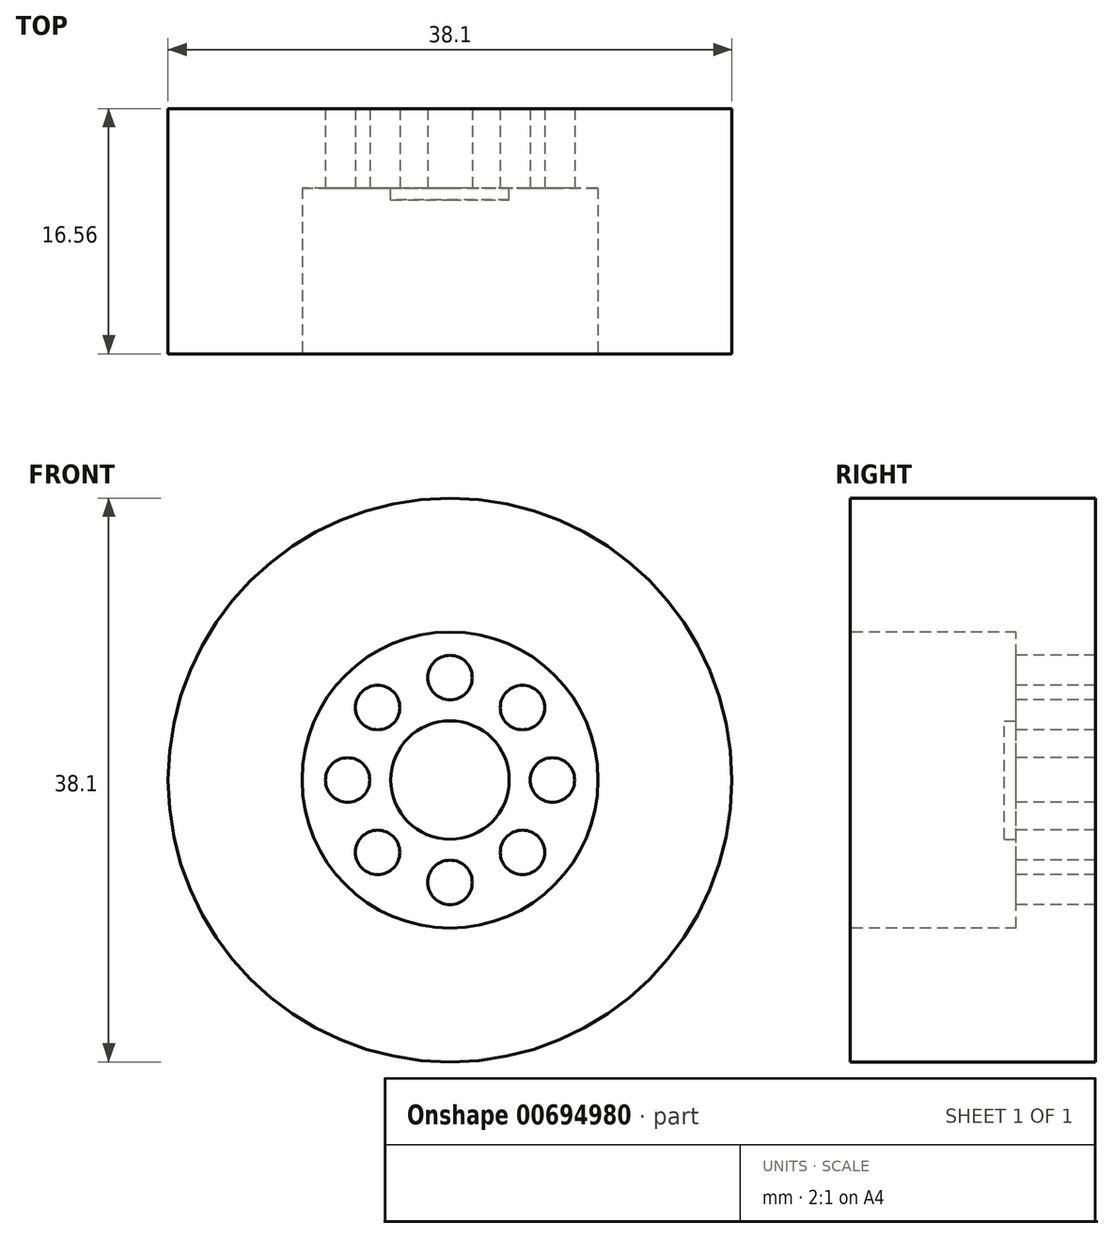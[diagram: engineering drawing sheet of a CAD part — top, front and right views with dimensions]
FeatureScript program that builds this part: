
annotation { "Feature Type Name" : "Feature", "Feature Type Description" : "" }
export const myFeature = defineFeature(function(context is Context, id is Id, definition is map)
    precondition{}
    {
        {
            var Q0;
            Q0=qCreatedBy(makeId("Front.planeOp"),FACE);
            var sketch = newSketch(context, id + "F0", { "sketchPlane" : qUnion([Q0])});
            skCircle(sketch, "E0", {"center": v(0, 0) * mm, "radius": 19.05 * mm});
            skSolve(sketch);
        }
        {
            var Q0;
            Q0=makeQuery(id+"F0.imprint","IMPRINT",FACE,{"disambiguationData":[TD([[makeQuery(id+"F0.imprint","IMPRINT",EDGE,{"derivedFrom":sQuery(id+"F0.wireOp",EDGE,"E0")}),1.0]])]});
            extrude(context, id + "F1", {"entities" : qUnion([Q0]), "depth" : 16.56 * mm, "offsetDistance" : 25.4 * mm});
        }
        {
            var Q0;
            Q0=makeQuery(id+"F1.opExtrude","CAP_FACE",FACE,{"disambiguationData":[OSD([sQuery(id+"F0.wireOp",EDGE,"E0")])],"isStart":false});
            var sketch = newSketch(context, id + "F2", { "sketchPlane" : qUnion([Q0])});
            skCircle(sketch, "E1", {"center": v(0, 0) * mm, "radius": 10 * mm});
            skSolve(sketch);
        }
        {
            var Q0;
            Q0=makeQuery(id+"F2.imprint","IMPRINT",FACE,{"disambiguationData":[TD([[makeQuery(id+"F2.imprint","IMPRINT",EDGE,{"derivedFrom":sQuery(id+"F2.wireOp",EDGE,"E1")}),1.0]])]});
            extrude(context, id + "F3", {"entities" : qUnion([Q0]), "operationType" : NewBodyOperationType.REMOVE, "oppositeDirection" : true, "depth" : 11.2 * mm, "offsetDistance" : 25 * mm});
        }
        {
            var Q0;
            Q0=makeQuery(id+"F3.boolean.opBoolean","COPY",FACE,{"derivedFrom":makeQuery(id+"F3.opExtrude","CAP_FACE",FACE,{"disambiguationData":[OSD([sQuery(id+"F2.wireOp",EDGE,"E1")])],"isStart":false})});
            var sketch = newSketch(context, id + "F4", { "sketchPlane" : qUnion([Q0])});
            skCircle(sketch, "E2", {"center": v(0, 0) * mm, "radius": 4 * mm});
            skSolve(sketch);
        }
        {
            var Q0;
            Q0 = qSketchRegion(id + "F4", true);
            extrude(context, id + "F5", {"entities" : qUnion([Q0]), "operationType" : NewBodyOperationType.ADD, "depth" : .8 * mm, "offsetDistance" : 25 * mm});
        }
        {
            var Q0;
            Q0=makeQuery(id+"F5.opExtrude","CAP_FACE",FACE,{"disambiguationData":[OSD([sQuery(id+"F4.wireOp",EDGE,"E2")])],"isStart":false});
            var sketch = newSketch(context, id + "F6", { "sketchPlane" : qUnion([Q0])});
            skCircle(sketch, "E3", {"center": v(0, 0) * mm, "radius": 0.93 * mm});
            skSolve(sketch);
        }
        {
            var Q0;
            Q0=sQuery(id+"F6.wireOp",EDGE,"E3");
            extrude(context, id + "F7", {"bodyType" : ToolBodyType.SURFACE, "surfaceEntities" : qUnion([Q0]), "depth" : 1.58 * mm, "offsetDistance" : 25 * mm});
        }
        {
            var Q0;
            Q0=makeQuery(id+"F3.boolean.opBoolean","COPY",FACE,{"derivedFrom":makeQuery(id+"F3.opExtrude","CAP_FACE",FACE,{"disambiguationData":[OSD([sQuery(id+"F2.wireOp",EDGE,"E1")])],"isStart":false})});
            var sketch = newSketch(context, id + "F8", { "sketchPlane" : qUnion([Q0])});
            skCircle(sketch, "E4", {"center": v(0, 6.92) * mm, "radius": 1.5 * mm});
            skCircle(sketch, "E5.1.0", {"center": v(-4.9, 4.9) * mm, "radius": 1.5 * mm});
            skCircle(sketch, "E5.2.0", {"center": v(-6.92, 0) * mm, "radius": 1.5 * mm});
            skPoint(sketch, "E5.center", {"position": v(0, 0) * mm});
            skCircle(sketch, "E6.1.3.0", {"center": v(-4.9, -4.9) * mm, "radius": 1.5 * mm});
            skCircle(sketch, "E6.1.4.0", {"center": v(0, -6.92) * mm, "radius": 1.5 * mm});
            skCircle(sketch, "E6.1.5.0", {"center": v(4.9, -4.9) * mm, "radius": 1.5 * mm});
            skCircle(sketch, "E6.1.6.0", {"center": v(6.92, 0) * mm, "radius": 1.5 * mm});
            skCircle(sketch, "E6.1.7.0", {"center": v(4.9, 4.9) * mm, "radius": 1.5 * mm});
            skSolve(sketch);
        }
        {
            var Q0;
            Q0=makeQuery(id+"F8.imprint","IMPRINT",FACE,{"disambiguationData":[TD([[makeQuery(id+"F8.imprint","IMPRINT",EDGE,{"derivedFrom":sQuery(id+"F8.wireOp",EDGE,"E4")}),1.0]])]});
            var Q1;
            Q1=makeQuery(id+"F8.imprint","IMPRINT",FACE,{"disambiguationData":[TD([[makeQuery(id+"F8.imprint","IMPRINT",EDGE,{"derivedFrom":sQuery(id+"F8.wireOp",EDGE,"E5.1.0")}),1.0]])]});
            var Q2;
            Q2=makeQuery(id+"F8.imprint","IMPRINT",FACE,{"disambiguationData":[TD([[makeQuery(id+"F8.imprint","IMPRINT",EDGE,{"derivedFrom":sQuery(id+"F8.wireOp",EDGE,"E5.2.0")}),1.0]])]});
            var Q3;
            Q3=makeQuery(id+"F8.imprint","IMPRINT",FACE,{"disambiguationData":[TD([[makeQuery(id+"F8.imprint","IMPRINT",EDGE,{"derivedFrom":sQuery(id+"F8.wireOp",EDGE,"E6.1.3.0")}),1.0]])]});
            var Q4;
            Q4=makeQuery(id+"F8.imprint","IMPRINT",FACE,{"disambiguationData":[TD([[makeQuery(id+"F8.imprint","IMPRINT",EDGE,{"derivedFrom":sQuery(id+"F8.wireOp",EDGE,"E6.1.4.0")}),1.0]])]});
            var Q5;
            Q5=makeQuery(id+"F8.imprint","IMPRINT",FACE,{"disambiguationData":[TD([[makeQuery(id+"F8.imprint","IMPRINT",EDGE,{"derivedFrom":sQuery(id+"F8.wireOp",EDGE,"E6.1.5.0")}),1.0]])]});
            var Q6;
            Q6=makeQuery(id+"F8.imprint","IMPRINT",FACE,{"disambiguationData":[TD([[makeQuery(id+"F8.imprint","IMPRINT",EDGE,{"derivedFrom":sQuery(id+"F8.wireOp",EDGE,"E6.1.6.0")}),1.0]])]});
            var Q7;
            Q7=makeQuery(id+"F8.imprint","IMPRINT",FACE,{"disambiguationData":[TD([[makeQuery(id+"F8.imprint","IMPRINT",EDGE,{"derivedFrom":sQuery(id+"F8.wireOp",EDGE,"E6.1.7.0")}),1.0]])]});
            var Q8;
            Q8=sQuery(id+"F8.wireOp",EDGE,"E4");
            extrude(context, id + "F9", {"entities" : qUnion([Q0, Q1, Q2, Q3, Q4, Q5, Q6, Q7]), "operationType" : NewBodyOperationType.REMOVE, "surfaceEntities" : qUnion([Q8]), "oppositeDirection" : true, "depth" : 6 * mm, "offsetDistance" : 25 * mm});
        }
    });
